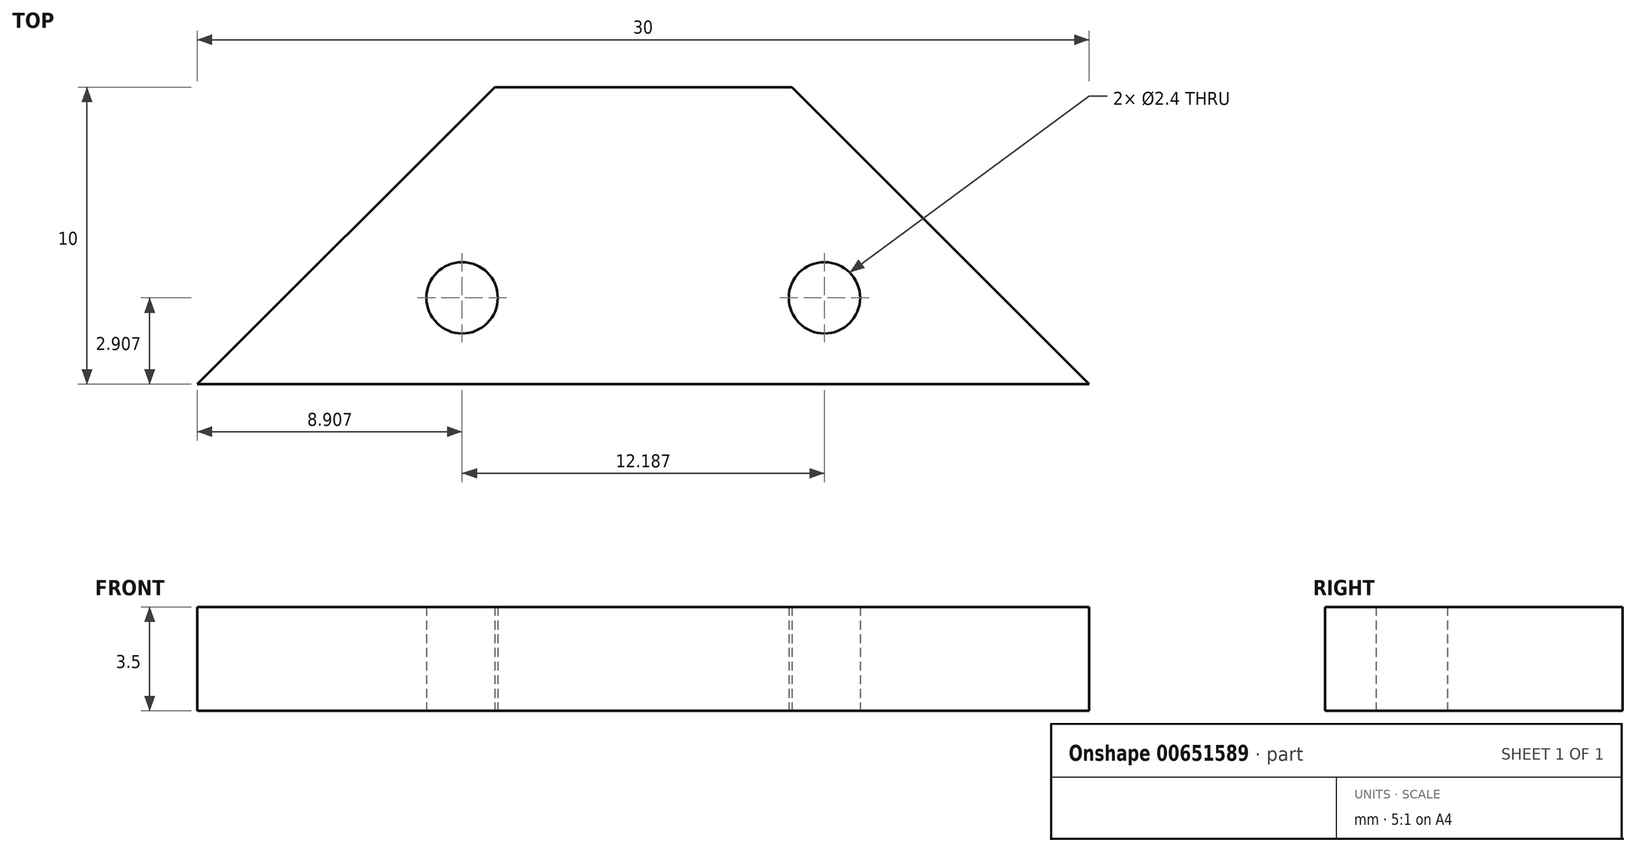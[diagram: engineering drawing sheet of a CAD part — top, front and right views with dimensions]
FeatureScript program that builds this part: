
annotation { "Feature Type Name" : "Feature", "Feature Type Description" : "" }
export const myFeature = defineFeature(function(context is Context, id is Id, definition is map)
    precondition{}
    {
        {
            var Q0;
            Q0=qCreatedBy(makeId("Top.planeOp"),FACE);
            var sketch = newSketch(context, id + "F0", { "sketchPlane" : qUnion([Q0])});
            skLineSegment(sketch, "E0.bottom", {"start": v(10, 5) * mm, "end": v(0, 5) * mm});
            skLineSegment(sketch, "E0.right", {"start": v(0, 5) * mm, "end": v(-10, -5) * mm});
            skPoint(sketch, "E0.middle", {"position": v(0, 0) * mm});
            skCircle(sketch, "E1", {"center": v(-1.1, -2.1) * mm, "radius": 1.2 * mm});
            skCircle(sketch, "E2", {"center": v(11.1, -2.1) * mm, "radius": 1.2 * mm});
            skLineSegment(sketch, "E3", {"start": v(11.1, -2.1) * mm, "end": v(17.1, -2.1) * mm, "construction": true});
            skLineSegment(sketch, "E4", {"start": v(-1.1, -2.1) * mm, "end": v(-7.1, -2.1) * mm, "construction": true});
            skLineSegment(sketch, "E5", {"start": v(10, 5) * mm, "end": v(20, -5) * mm});
            skLineSegment(sketch, "E6", {"start": v(-10, -5) * mm, "end": v(20, -5) * mm});
            skLineSegment(sketch, "E7", {"start": v(-1.1, -2.1) * mm, "end": v(11.1, -2.1) * mm, "construction": true});
            skSolve(sketch);
        }
        {
            var Q0;
            Q0=qSketchRegion(id+"F0",true);
            extrude(context, id + "F1", {"entities" : qUnion([Q0]), "depth" : 3.5 * mm});
        }
        {
            var Q0;
            Q0=makeQuery(id+"F1.opExtrude","SWEPT_BODY",BODY,{"disambiguationData":[OSD([sQuery(id+"F0.wireOp",EDGE,"E0.bottom"),sQuery(id+"F0.wireOp",EDGE,"E0.right"),sQuery(id+"F0.wireOp",EDGE,"E1"),sQuery(id+"F0.wireOp",EDGE,"E2"),sQuery(id+"F0.wireOp",EDGE,"E5"),sQuery(id+"F0.wireOp",EDGE,"E6")])]});
            transform(context, id + "F2", {"entities" : qUnion([Q0]), "transformType" : TransformType.TRANSLATION_3D, "dx" : 0 * mm, "dy" : 0 * mm, "dz" : 0 * mm, "makeCopy" : true});
        }
        {
            var Q0;
            Q0=makeQuery(id+"F1.opExtrude","SWEPT_BODY",BODY,{"disambiguationData":[OSD([sQuery(id+"F0.wireOp",EDGE,"E0.bottom"),sQuery(id+"F0.wireOp",EDGE,"E0.right"),sQuery(id+"F0.wireOp",EDGE,"E1"),sQuery(id+"F0.wireOp",EDGE,"E2"),sQuery(id+"F0.wireOp",EDGE,"E5"),sQuery(id+"F0.wireOp",EDGE,"E6")])]});
            deleteBodies(context, id + "F3", {"entities" : qUnion([Q0])});
        }
    });
